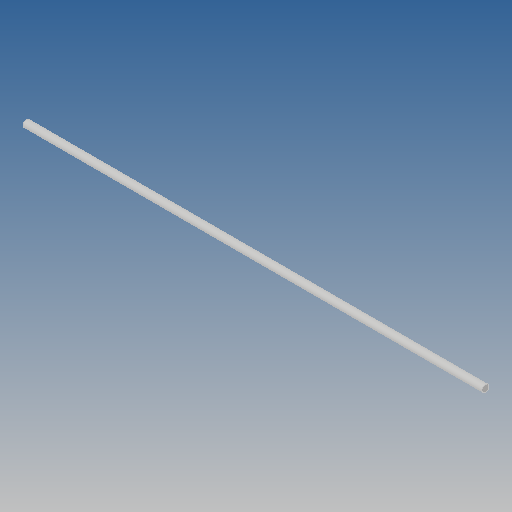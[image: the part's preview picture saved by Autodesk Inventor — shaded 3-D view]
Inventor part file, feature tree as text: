
AUTODESK INVENTOR PART (.ipt)
format: ipt  version: 2018 (Build 220112000, 112)  size: 77,312 bytes
history: native  units: mm
features: other x1, extrude x1, sketch x1
ambient origin geometry x8: Origin, YZ Plane, XZ Plane, XY Plane, X Axis, Y Axis, Z Axis, Center Point
bodies: Solid1 (feature_tree)
feature tree (3):
  other  "<userpath>\OneDrive\Objet3D\3DPrinter\Parameters.xlsx"
  extrude  "Extrusion1"  Depth=500.0mm TaperAngle=0.0deg
  sketch  "Sketch1"  dims[d0=8.0mm d1=500.0mm d2=0.0mm]
